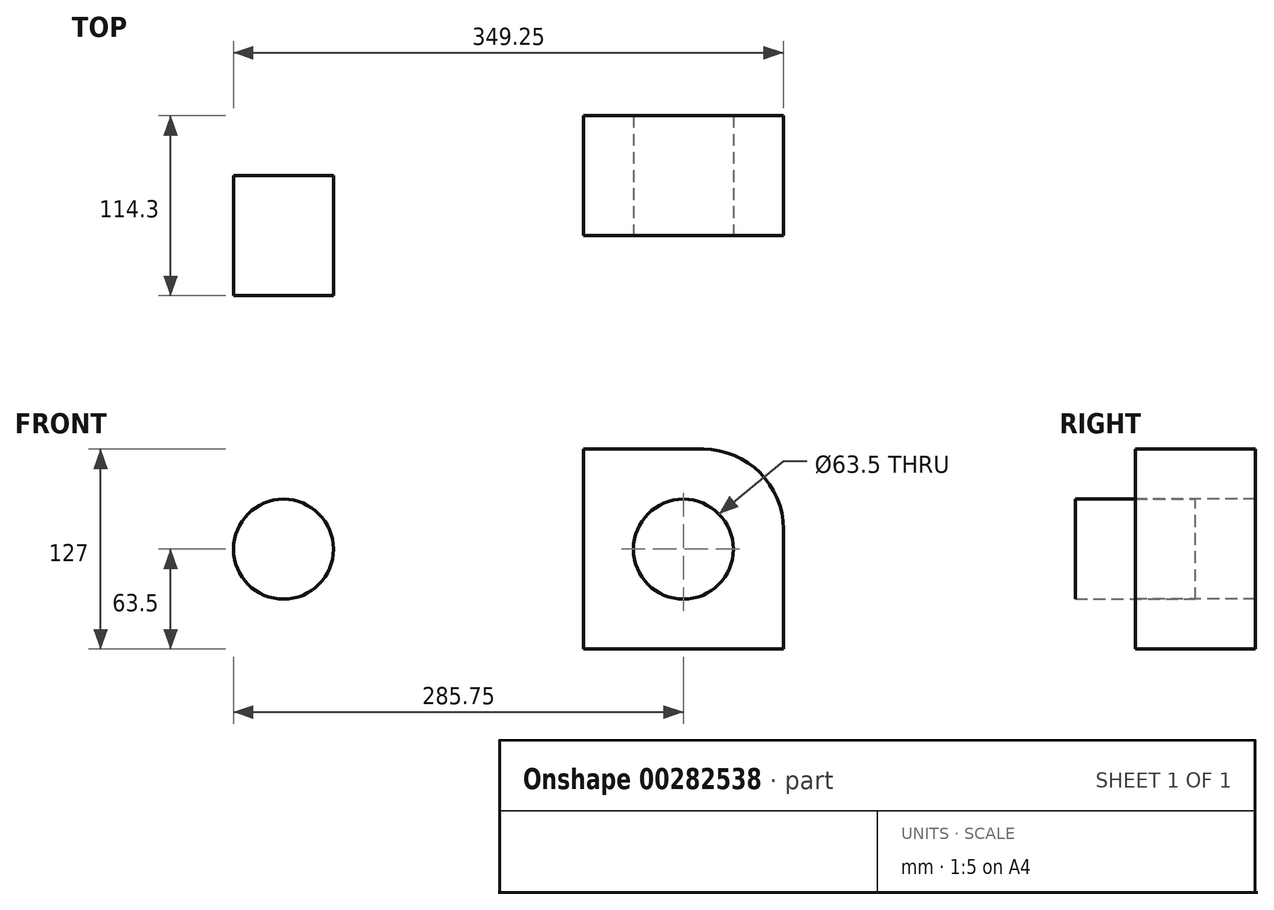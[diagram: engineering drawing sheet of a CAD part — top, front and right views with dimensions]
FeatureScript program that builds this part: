
annotation { "Feature Type Name" : "Feature", "Feature Type Description" : "" }
export const myFeature = defineFeature(function(context is Context, id is Id, definition is map)
    precondition{}
    {
        {
            var Q0;
            Q0=qCreatedBy(makeId("Top.planeOp"),FACE);
            var sketch = newSketch(context, id + "F0", { "sketchPlane" : qUnion([Q0])});
            skLineSegment(sketch, "E0.bottom", {"start": v(-63.5, 38.1) * mm, "end": v(63.5, 38.1) * mm});
            skLineSegment(sketch, "E0.top", {"start": v(-63.5, -38.1) * mm, "end": v(63.5, -38.1) * mm});
            skLineSegment(sketch, "E0.left", {"start": v(-63.5, 38.1) * mm, "end": v(-63.5, -38.1) * mm});
            skLineSegment(sketch, "E0.right", {"start": v(63.5, 38.1) * mm, "end": v(63.5, -38.1) * mm});
            skPoint(sketch, "E0.middle", {"position": v(0, 0) * mm});
            skSolve(sketch);
        }
        {
            var Q0;
            Q0 = qSketchRegion(id + "F0", true);
            extrude(context, id + "F1", {"entities" : qUnion([Q0]), "endBound" : BoundingType.SYMMETRIC, "depth" : 127 * mm});
        }
        {
            var Q0;
            Q0=makeQuery(id+"F1.opExtrude","CAP_EDGE",EDGE,{"disambiguationData":[OSD([sQuery(id+"F0.wireOp",EDGE,"E0.right")])],"isStart":false});
            fillet(context, id + "F2", {"entities" : qUnion([Q0]), "radius" : 50.8 * mm, "tangentPropagation" : true, "allowEdgeOverflow" : false});
        }
        {
            var Q0;
            Q0=makeQuery(id+"F1.opExtrude","SWEPT_FACE",FACE,{"disambiguationData":[OSD([sQuery(id+"F0.wireOp",EDGE,"E0.top")])]});
            var sketch = newSketch(context, id + "F3", { "sketchPlane" : qUnion([Q0])});
            skCircle(sketch, "E1", {"center": v(0, 0) * mm, "radius": 31.75 * mm});
            skSolve(sketch);
        }
        {
            var Q0;
            Q0=makeQuery(id+"F3.imprint","IMPRINT",FACE,{"disambiguationData":[TD([[makeQuery(id+"F3.imprint","IMPRINT",EDGE,{"derivedFrom":sQuery(id+"F3.wireOp",EDGE,"E1")}),1.0]])]});
            extrude(context, id + "F4", {"entities" : qUnion([Q0]), "operationType" : NewBodyOperationType.REMOVE, "endBound" : BoundingType.THROUGH_ALL, "oppositeDirection" : true, "depth" : 25.4 * mm});
        }
        {
            var Q0;
            Q0=makeQuery(id+"F1.opExtrude","SWEPT_FACE",FACE,{"disambiguationData":[OSD([sQuery(id+"F0.wireOp",EDGE,"E0.top")])]});
            var sketch = newSketch(context, id + "F5", { "sketchPlane" : qUnion([Q0])});
            skCircle(sketch, "E2", {"center": v(-254, 0) * mm, "radius": 31.75 * mm});
            skSolve(sketch);
        }
        {
            var Q0;
            Q0=makeQuery(id+"F5.imprint","IMPRINT",FACE,{"disambiguationData":[TD([[makeQuery(id+"F5.imprint","IMPRINT",EDGE,{"derivedFrom":sQuery(id+"F5.wireOp",EDGE,"E2")}),1.0]])]});
            extrude(context, id + "F6", {"entities" : qUnion([Q0]), "endBound" : BoundingType.SYMMETRIC, "depth" : 76.2 * mm});
        }
    });
